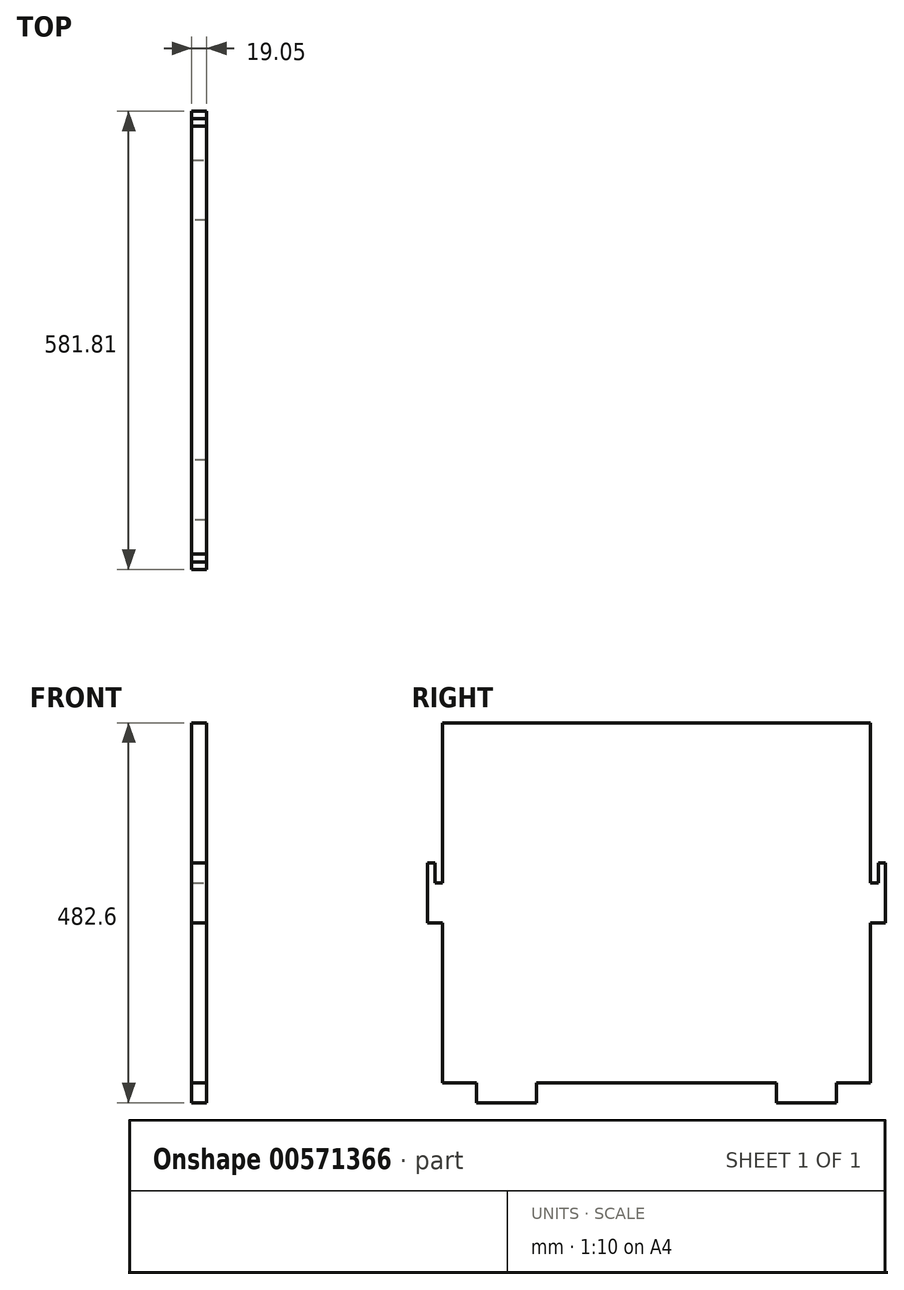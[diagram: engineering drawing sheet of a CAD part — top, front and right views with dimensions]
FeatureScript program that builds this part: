
annotation { "Feature Type Name" : "Feature", "Feature Type Description" : "" }
export const myFeature = defineFeature(function(context is Context, id is Id, definition is map)
    precondition{}
    {
        {
            var Q0;
            Q0=qCreatedBy(makeId("Top.planeOp"),FACE);
            var sketch = newSketch(context, id + "F0", { "sketchPlane" : qUnion([Q0])});
            skLineSegment(sketch, "E0.bottom", {"start": v(-32.27, 544.57) * mm, "end": v(-13.22, 544.57) * mm});
            skLineSegment(sketch, "E0.top", {"start": v(-32.27, 1.01) * mm, "end": v(-13.22, 1.01) * mm});
            skLineSegment(sketch, "E0.left", {"start": v(-32.27, 544.57) * mm, "end": v(-32.27, 1.01) * mm});
            skLineSegment(sketch, "E0.right", {"start": v(-13.22, 544.57) * mm, "end": v(-13.22, 1.01) * mm});
            skSolve(sketch);
        }
        {
            var Q0;
            Q0=makeQuery(id+"F0.imprint","IMPRINT",FACE,{"disambiguationData":[TD([[makeQuery(id+"F0.imprint","IMPRINT",EDGE,{"derivedFrom":sQuery(id+"F0.wireOp",EDGE,"E0.bottom")}),-1.0]])]});
            extrude(context, id + "F1", {"entities" : qUnion([Q0]), "depth" : 457.2 * mm, "offsetDistance" : 25.4 * mm});
        }
        {
            var Q0;
            Q0=makeQuery(id+"F1.opExtrude","SWEPT_FACE",FACE,{"disambiguationData":[OSD([sQuery(id+"F0.wireOp",EDGE,"E0.bottom")])]});
            var sketch = newSketch(context, id + "F2", { "sketchPlane" : qUnion([Q0])});
            skLineSegment(sketch, "E1", {"start": v(13.22, 254) * mm, "end": v(32.27, 254) * mm});
            skLineSegment(sketch, "E2", {"start": v(13.22, 203.2) * mm, "end": v(32.27, 203.2) * mm});
            skLineSegment(sketch, "E3.0", {"start": v(13.22, 457.2) * mm, "end": v(13.22, 0) * mm});
            skLineSegment(sketch, "E4.0", {"start": v(32.27, 457.2) * mm, "end": v(32.27, 0) * mm});
            skLineSegment(sketch, "E5.0", {"start": v(32.27, 0) * mm, "end": v(13.22, 0) * mm});
            skSolve(sketch);
        }
        {
            var Q0;
            {var subQ0=sQuery(id+"F2.wireOp",EDGE,"E1");Q0=makeQuery(id+"F2.imprint","IMPRINT",FACE,{"disambiguationData":[TD([[makeQuery(id+"F2.imprint","IMPRINT",EDGE,{"derivedFrom":subQ0}),-1.0]])]});}
            extrude(context, id + "F3", {"entities" : qUnion([Q0]), "operationType" : NewBodyOperationType.ADD, "depth" : 19.13 * mm, "offsetDistance" : 25.4 * mm});
        }
        {
            var Q0;
            Q0=makeQuery(id+"F3.opExtrude","SWEPT_FACE",FACE,{"disambiguationData":[OSD([sQuery(id+"F2.wireOp",EDGE,"E1")])]});
            var sketch = newSketch(context, id + "F4", { "sketchPlane" : qUnion([Q0])});
            skLineSegment(sketch, "E6.0", {"start": v(-13.22, 563.7) * mm, "end": v(-13.22, 544.57) * mm});
            skLineSegment(sketch, "E7.0", {"start": v(-32.27, 563.7) * mm, "end": v(-32.27, 544.57) * mm});
            skLineSegment(sketch, "E8", {"start": v(-13.22, 554.17) * mm, "end": v(-32.27, 554.17) * mm});
            skLineSegment(sketch, "E9.0.1", {"start": v(-13.22, 563.7) * mm, "end": v(-32.27, 563.7) * mm});
            skLineSegment(sketch, "E9.0.3", {"start": v(-32.27, 563.7) * mm, "end": v(-13.22, 563.7) * mm});
            skSolve(sketch);
        }
        {
            var Q0;
            {var subQ2=sQuery(id+"F4.wireOp",EDGE,"E8");Q0=makeQuery(id+"F4.imprint","IMPRINT",FACE,{"disambiguationData":[TD([[makeQuery(id+"F4.imprint","IMPRINT",EDGE,{"derivedFrom":subQ2}),-1.0]])]});}
            extrude(context, id + "F5", {"entities" : qUnion([Q0]), "operationType" : NewBodyOperationType.ADD, "depth" : 25.4 * mm, "offsetDistance" : 25.4 * mm});
        }
        {
            var Q0;
            Q0=makeQuery(id+"F1.opExtrude","SWEPT_FACE",FACE,{"disambiguationData":[OSD([sQuery(id+"F0.wireOp",EDGE,"E0.top")])]});
            var sketch = newSketch(context, id + "F6", { "sketchPlane" : qUnion([Q0])});
            skLineSegment(sketch, "E10", {"start": v(-32.27, 254) * mm, "end": v(-13.22, 254) * mm});
            skLineSegment(sketch, "E11", {"start": v(-32.27, 203.2) * mm, "end": v(-13.22, 203.2) * mm});
            skSolve(sketch);
        }
        {
            var Q0;
            {var subQ0=sQuery(id+"F6.wireOp",EDGE,"E10");Q0=makeQuery(id+"F6.imprint","IMPRINT",FACE,{"disambiguationData":[TD([[makeQuery(id+"F6.imprint","IMPRINT",EDGE,{"derivedFrom":subQ0}),-1.0]])]});}
            extrude(context, id + "F7", {"entities" : qUnion([Q0]), "operationType" : NewBodyOperationType.ADD, "depth" : 19.13 * mm, "offsetDistance" : 25.4 * mm});
        }
        {
            var Q0;
            Q0=makeQuery(id+"F7.opExtrude","SWEPT_FACE",FACE,{"disambiguationData":[OSD([sQuery(id+"F6.wireOp",EDGE,"E10")])]});
            var sketch = newSketch(context, id + "F8", { "sketchPlane" : qUnion([Q0])});
            skLineSegment(sketch, "E12", {"start": v(-32.27, -8.59) * mm, "end": v(-13.22, -8.59) * mm});
            skSolve(sketch);
        }
        {
            var Q0;
            {var subQ0=sQuery(id+"F8.wireOp",EDGE,"E12");Q0=makeQuery(id+"F8.imprint","IMPRINT",FACE,{"disambiguationData":[TD([[makeQuery(id+"F8.imprint","IMPRINT",EDGE,{"derivedFrom":subQ0}),-1.0]])]});}
            extrude(context, id + "F9", {"entities" : qUnion([Q0]), "operationType" : NewBodyOperationType.ADD, "depth" : 25.4 * mm, "offsetDistance" : 25.4 * mm});
        }
        {
            var Q0;
            Q0=makeQuery(id+"F1.opExtrude","CAP_FACE",FACE,{"disambiguationData":[OSD([sQuery(id+"F0.wireOp",EDGE,"E0.bottom"),sQuery(id+"F0.wireOp",EDGE,"E0.top"),sQuery(id+"F0.wireOp",EDGE,"E0.left"),sQuery(id+"F0.wireOp",EDGE,"E0.right")])],"isStart":true});
            var sketch = newSketch(context, id + "F10", { "sketchPlane" : qUnion([Q0])});
            skLineSegment(sketch, "E13", {"start": v(-13.22, -1.01) * mm, "end": v(-32.27, -1.01) * mm});
            skLineSegment(sketch, "E14", {"start": v(-13.22, -544.57) * mm, "end": v(-32.27, -544.57) * mm});
            skLineSegment(sketch, "E15", {"start": v(-13.22, -120.4) * mm, "end": v(-32.27, -120.4) * mm});
            skLineSegment(sketch, "E16", {"start": v(-13.22, -120.4) * mm, "end": v(-13.22, -44.2) * mm});
            skLineSegment(sketch, "E17", {"start": v(-13.22, -44.2) * mm, "end": v(-32.27, -44.2) * mm});
            skLineSegment(sketch, "E18", {"start": v(-32.27, -44.2) * mm, "end": v(-32.27, -120.4) * mm});
            skLineSegment(sketch, "E19", {"start": v(-13.22, -425.2) * mm, "end": v(-32.27, -425.2) * mm});
            skLineSegment(sketch, "E20", {"start": v(-32.27, -425.2) * mm, "end": v(-32.27, -501.4) * mm});
            skLineSegment(sketch, "E21", {"start": v(-32.27, -501.4) * mm, "end": v(-13.22, -501.4) * mm});
            skLineSegment(sketch, "E22", {"start": v(-13.22, -501.4) * mm, "end": v(-13.22, -425.2) * mm});
            skSolve(sketch);
        }
        {
            var Q0;
            Q0 = qSketchRegion(id + "F10", true);
            var Q1;
            Q1=makeQuery(id+"F10.imprint","IMPRINT",FACE,{"disambiguationData":[TD([[makeQuery(id+"F10.imprint","IMPRINT",EDGE,{"derivedFrom":sQuery(id+"F10.wireOp",EDGE,"Jk6SSUgD-5o10-eRuT-4fbJ-PHhFEYMPNGny")}),1.0]])]});
            extrude(context, id + "F11", {"entities" : qUnion([Q0, Q1]), "operationType" : NewBodyOperationType.ADD, "depth" : 9.65 * mm, "offsetDistance" : 25.4 * mm});
        }
        {
            var Q0;
            Q0 = qSketchRegion(id + "F10", true);
            var Q1;
            Q1=makeQuery(id+"F11.opExtrude","CAP_FACE",FACE,{"disambiguationData":[OSD([sQuery(id+"F10.wireOp",EDGE,"RdSJn8x7-9hNZ-0bgu-hCth-5MuYVsukvWJt"),sQuery(id+"F10.wireOp",EDGE,"IvFeOphQ-nbdy-IWnW-gyE4-l4uNIZhi4Q3S"),sQuery(id+"F10.wireOp",EDGE,"bS1t9jwx-nNfB-QTes-0HaN-d5l0ltNsypmi"),sQuery(id+"F10.wireOp",EDGE,"GE3w4s52-YCB2-dMdU-Lpe0-kp2GtBdkyB8E")])],"isStart":false});
            extrude(context, id + "F12", {"entities" : qUnion([Q0, Q1]), "operationType" : NewBodyOperationType.ADD, "depth" : 25.4 * mm, "offsetDistance" : 25.4 * mm});
        }
    });
